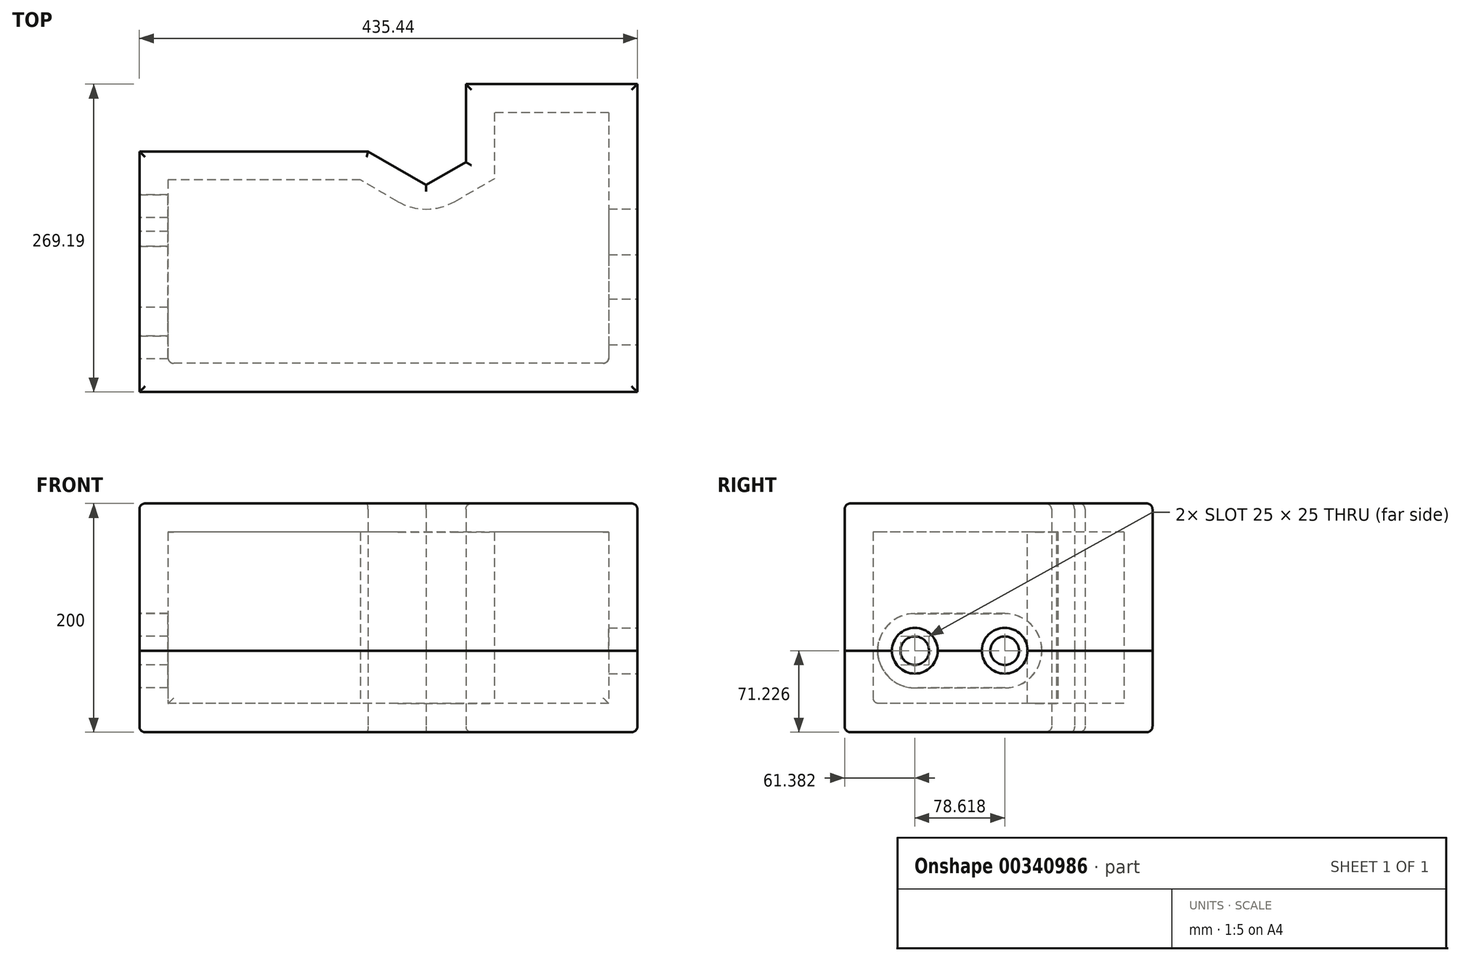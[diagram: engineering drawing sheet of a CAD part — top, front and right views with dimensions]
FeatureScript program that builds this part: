
annotation { "Feature Type Name" : "Feature", "Feature Type Description" : "" }
export const myFeature = defineFeature(function(context is Context, id is Id, definition is map)
    precondition{}
    {
        {
            var Q0;
            Q0=qCreatedBy(makeId("Top.planeOp"),FACE);
            var sketch = newSketch(context, id + "F0", { "sketchPlane" : qUnion([Q0])});
            skLineSegment(sketch, "E0.top", {"start": v(217.72, -95) * mm, "end": v(-217.72, -95) * mm});
            skLineSegment(sketch, "E0.left", {"start": v(217.72, 95) * mm, "end": v(217.72, -95) * mm});
            skLineSegment(sketch, "E0.right", {"start": v(-217.72, 95) * mm, "end": v(-217.72, -95) * mm});
            skPoint(sketch, "E0.middle", {"position": v(0, 0) * mm});
            skLineSegment(sketch, "E1", {"start": v(217.72, 174.19) * mm, "end": v(217.72, 95) * mm});
            skLineSegment(sketch, "E2", {"start": v(33.07, 86) * mm, "end": v(67.72, 106) * mm});
            skLineSegment(sketch, "E3", {"start": v(33.07, 86) * mm, "end": v(61.6, 86) * mm, "construction": true});
            skLineSegment(sketch, "E4", {"start": v(67.72, 106) * mm, "end": v(131.32, 106) * mm, "construction": true});
            skLineSegment(sketch, "E5", {"start": v(217.72, 174.19) * mm, "end": v(67.72, 174.19) * mm});
            skLineSegment(sketch, "E6", {"start": v(67.72, 174.19) * mm, "end": v(67.72, 106) * mm});
            skLineSegment(sketch, "E7", {"start": v(67.72, 106) * mm, "end": v(217.72, 106) * mm, "construction": true});
            skLineSegment(sketch, "E8", {"start": v(33.07, 86) * mm, "end": v(-17.72, 115.31) * mm});
            skLineSegment(sketch, "E9", {"start": v(33.07, 86) * mm, "end": v(7.07, 86) * mm, "construction": true});
            skLineSegment(sketch, "E10", {"start": v(-17.72, 115.31) * mm, "end": v(-217.72, 115.31) * mm});
            skLineSegment(sketch, "E11", {"start": v(-217.72, 115.31) * mm, "end": v(-217.72, 95) * mm});
            skSolve(sketch);
        }
        {
            var Q0;
            Q0=makeQuery(id+"F0.imprint","IMPRINT",FACE,{"disambiguationData":[TD([[makeQuery(id+"F0.imprint","IMPRINT",EDGE,{"derivedFrom":sQuery(id+"F0.wireOp",EDGE,"E0.top")}),-1.0]])]});
            extrude(context, id + "F1", {"entities" : qUnion([Q0]), "depth" : 200 * mm});
        }
        {
            var Q0;
            Q0=makeQuery(id+"F1.opExtrude","CAP_FACE",FACE,{"disambiguationData":[OSD([sQuery(id+"F0.wireOp",EDGE,"E0.bottom"),sQuery(id+"F0.wireOp",EDGE,"E0.top"),sQuery(id+"F0.wireOp",EDGE,"E0.left"),sQuery(id+"F0.wireOp",EDGE,"E0.right")])],"isStart":false});
            shell(context, id + "F2", {"entities" : qUnion([Q0]), "thickness" : 25 * mm});
        }
        {
            var Q0;
            Q0=makeQuery(id+"F1.opExtrude","SWEPT_FACE",FACE,{"disambiguationData":[OSD([sQuery(id+"F0.wireOp",EDGE,"E0.left")])]});
            var sketch = newSketch(context, id + "F3", { "sketchPlane" : qUnion([Q0])});
            skCircle(sketch, "E12", {"center": v(45, 71.23) * mm, "radius": 20 * mm});
            skCircle(sketch, "E13", {"center": v(-33.62, 71.23) * mm, "radius": 20 * mm});
            skLineSegment(sketch, "E14", {"start": v(-33.62, 71.23) * mm, "end": v(45, 71.23) * mm, "construction": true});
            skLineSegment(sketch, "E15", {"start": v(5.7, 71.23) * mm, "end": v(5.7, 0) * mm, "construction": true});
            skLineSegment(sketch, "E16", {"start": v(-33.62, 71.23) * mm, "end": v(-95, 71.23) * mm, "construction": true});
            skSolve(sketch);
        }
        {
            var Q0;
            Q0 = qSketchRegion(id + "F3", true);
            extrude(context, id + "F4", {"entities" : qUnion([Q0]), "operationType" : NewBodyOperationType.REMOVE, "oppositeDirection" : true, "depth" : 25 * mm});
        }
        {
            var Q0;
            Q0=makeQuery(id+"F2.opShell","OFFSET_FACE",FACE,{"disambiguationData":[OSD([sQuery(id+"F0.wireOp",EDGE,"E0.bottom"),sQuery(id+"F0.wireOp",EDGE,"E0.top"),sQuery(id+"F0.wireOp",EDGE,"E0.left"),sQuery(id+"F0.wireOp",EDGE,"E0.right")])]});
            var Q1;
            Q1=makeQuery(id+"F1.opExtrude","CAP_FACE",FACE,{"disambiguationData":[OSD([sQuery(id+"F0.wireOp",EDGE,"E0.bottom"),sQuery(id+"F0.wireOp",EDGE,"E0.top"),sQuery(id+"F0.wireOp",EDGE,"E0.left"),sQuery(id+"F0.wireOp",EDGE,"E0.right")])],"isStart":false});
            var Q2;
            Q2=makeQuery(id+"F1.opExtrude","CAP_FACE",FACE,{"disambiguationData":[OSD([sQuery(id+"F0.wireOp",EDGE,"E0.bottom"),sQuery(id+"F0.wireOp",EDGE,"E0.top"),sQuery(id+"F0.wireOp",EDGE,"E0.left"),sQuery(id+"F0.wireOp",EDGE,"E0.right")])],"isStart":true});
            fillet(context, id + "F5", {"entities" : qUnion([Q0, Q1, Q2]), "radius" : 5 * mm, "tangentPropagation" : true, "allowEdgeOverflow" : false});
        }
        {
            var Q0;
            Q0=makeQuery(id+"F1.opExtrude","SWEPT_FACE",FACE,{"disambiguationData":[OSD([sQuery(id+"F0.wireOp",EDGE,"E0.right")])]});
            var sketch = newSketch(context, id + "F6", { "sketchPlane" : qUnion([Q0])});
            skCircle(sketch, "E17", {"center": v(-45, 71.23) * mm, "radius": 12.5 * mm});
            skCircle(sketch, "E18", {"center": v(33.62, 71.23) * mm, "radius": 12.5 * mm});
            skSolve(sketch);
        }
        {
            var Q0;
            Q0 = qSketchRegion(id + "F6", true);
            extrude(context, id + "F7", {"entities" : qUnion([Q0]), "operationType" : NewBodyOperationType.REMOVE, "oppositeDirection" : true, "depth" : 25 * mm});
        }
        {
            var Q0;
            Q0=makeQuery(id+"F1.opExtrude","SWEPT_FACE",FACE,{"disambiguationData":[OSD([sQuery(id+"F0.wireOp",EDGE,"E0.top")])]});
            var sketch = newSketch(context, id + "F8", { "sketchPlane" : qUnion([Q0])});
            skPoint(sketch, "E19.middle", {"position": v(13.46, 71.23) * mm});
            skLineSegment(sketch, "E20", {"start": v(66.8, 71.23) * mm, "end": v(13.46, 71.23) * mm, "construction": true});
            skLineSegment(sketch, "E21", {"start": v(13.46, 0) * mm, "end": v(13.46, 71.23) * mm, "construction": true});
            skLineSegment(sketch, "E22.bottom", {"start": v(271.45, 71.28) * mm, "end": v(-244.53, 71.28) * mm});
            skLineSegment(sketch, "E22.top", {"start": v(271.45, 71.18) * mm, "end": v(-244.53, 71.18) * mm});
            skLineSegment(sketch, "E22.left", {"start": v(271.45, 71.28) * mm, "end": v(271.45, 71.18) * mm});
            skLineSegment(sketch, "E22.right", {"start": v(-244.53, 71.28) * mm, "end": v(-244.53, 71.18) * mm});
            skSolve(sketch);
        }
        {
            var Q0;
            Q0 = qSketchRegion(id + "F8", true);
            extrude(context, id + "F9", {"entities" : qUnion([Q0]), "operationType" : NewBodyOperationType.REMOVE, "oppositeDirection" : true, "depth" : 500 * mm});
        }
        {
            var Q0;
            Q0=makeQuery(id+"F1.opExtrude","CAP_FACE",FACE,{"disambiguationData":[OSD([sQuery(id+"F0.wireOp",EDGE,"E0.top"),sQuery(id+"F0.wireOp",EDGE,"E0.left"),sQuery(id+"F0.wireOp",EDGE,"E0.right"),sQuery(id+"F0.wireOp",EDGE,"E1"),sQuery(id+"F0.wireOp",EDGE,"E2"),sQuery(id+"F0.wireOp",EDGE,"E5"),sQuery(id+"F0.wireOp",EDGE,"E6"),sQuery(id+"F0.wireOp",EDGE,"E8"),sQuery(id+"F0.wireOp",EDGE,"E10"),sQuery(id+"F0.wireOp",EDGE,"E11")])],"isStart":false});
            var sketch = newSketch(context, id + "F10", { "sketchPlane" : qUnion([Q0])});
            skLineSegment(sketch, "E23", {"start": v(-212.72, -90) * mm, "end": v(-197.72, 95.31) * mm});
            skLineSegment(sketch, "E24", {"start": v(-197.72, 95.31) * mm, "end": v(-23.07, 95.31) * mm});
            skLineSegment(sketch, "E25", {"start": v(-23.07, 95.31) * mm, "end": v(33.07, 62.9) * mm});
            skLineSegment(sketch, "E26", {"start": v(33.07, 62.9) * mm, "end": v(87.72, 94.44) * mm});
            skLineSegment(sketch, "E27", {"start": v(87.72, 94.44) * mm, "end": v(87.72, 154.19) * mm});
            skLineSegment(sketch, "E28", {"start": v(87.72, 154.19) * mm, "end": v(197.72, 154.19) * mm});
            skLineSegment(sketch, "E29", {"start": v(197.72, 154.19) * mm, "end": v(197.72, -75) * mm});
            skLineSegment(sketch, "E30", {"start": v(197.72, -75) * mm, "end": v(-212.72, -90) * mm});
            skSolve(sketch);
        }
        {
            var Q0;
            Q0 = qSketchRegion(id + "F10", true);
            extrude(context, id + "F11", {"entities" : qUnion([Q0]), "operationType" : NewBodyOperationType.ADD, "oppositeDirection" : true, "depth" : 25 * mm});
        }
        {
            var Q0;
            {var subQ0=sQuery(id+"F0.wireOp",EDGE,"E8");var subQ1=sQuery(id+"F0.wireOp",EDGE,"E2");Q0=makeQuery(id+"F9.boolean.opBoolean","SPLIT",EDGE,{"disambiguationData":[TD([makeQuery(id+"F9.opExtrude","SWEPT_FACE",FACE,{"disambiguationData":[OSD([sQuery(id+"F8.wireOp",EDGE,"E22.top")])]})])],"derivedFrom":makeQuery(id+"F2.opShell","OFFSET_EDGE",EDGE,{"disambiguationData":[OSD([subQ1,subQ0])]})});}
            var Q1;
            {var subQ0=sQuery(id+"F0.wireOp",EDGE,"E8");var subQ1=sQuery(id+"F0.wireOp",EDGE,"E2");Q1=makeQuery(id+"F9.boolean.opBoolean","SPLIT",EDGE,{"disambiguationData":[TD([makeQuery(id+"F9.opExtrude","SWEPT_FACE",FACE,{"disambiguationData":[OSD([sQuery(id+"F8.wireOp",EDGE,"E22.bottom")])]})])],"derivedFrom":makeQuery(id+"F2.opShell","OFFSET_EDGE",EDGE,{"disambiguationData":[OSD([subQ1,subQ0])]})});}
            fillet(context, id + "F12", {"entities" : qUnion([Q0, Q1]), "radius" : 50 * mm, "tangentPropagation" : true, "allowEdgeOverflow" : false});
        }
        {
            var Q0;
            {var subQ0=sQuery(id+"F0.wireOp",EDGE,"E11");var subQ1=sQuery(id+"F0.wireOp",EDGE,"E0.right");Q0=makeQuery(id+"F9.boolean.opBoolean","SPLIT",FACE,{"disambiguationData":[TD([makeQuery(id+"F9.opExtrude","SWEPT_FACE",FACE,{"disambiguationData":[OSD([sQuery(id+"F8.wireOp",EDGE,"E22.bottom")])]})])],"derivedFrom":makeQuery(id+"F1.opExtrude","SWEPT_FACE",FACE,{"disambiguationData":[OSD([subQ1,subQ0])]})});}
            var sketch = newSketch(context, id + "F13", { "sketchPlane" : qUnion([Q0])});
            skArc(sketch, "E31", {"start": v(-45, 103.66) * mm, "mid": v(-77.43, 71.4) * mm, "end": v(-45.36, 38.8) * mm});
            skLineSegment(sketch, "E32", {"start": v(-45, 103.66) * mm, "end": v(33.62, 103.65) * mm});
            skPoint(sketch, "E32.endSnap0", {"position": v(33.62, 83.73) * mm});
            skArc(sketch, "E33", {"start": v(33.62, 38.8) * mm, "mid": v(66.05, 71.23) * mm, "end": v(33.62, 103.65) * mm});
            skLineSegment(sketch, "E34", {"start": v(-45.36, 38.8) * mm, "end": v(33.62, 38.8) * mm});
            skArc(sketch, "E35.0", {"start": v(-45, 103.76) * mm, "mid": v(-77.53, 71.4) * mm, "end": v(-45.36, 38.7) * mm});
            skLineSegment(sketch, "E35.1", {"start": v(-45, 103.76) * mm, "end": v(33.62, 103.75) * mm});
            skArc(sketch, "E35.2", {"start": v(33.62, 38.7) * mm, "mid": v(66.15, 71.23) * mm, "end": v(33.62, 103.75) * mm});
            skLineSegment(sketch, "E35.3", {"start": v(-45.36, 38.7) * mm, "end": v(33.62, 38.7) * mm});
            skSolve(sketch);
        }
        {
            var Q0;
            Q0 = qSketchRegion(id + "F13", true);
            extrude(context, id + "F14", {"entities" : qUnion([Q0]), "operationType" : NewBodyOperationType.REMOVE, "oppositeDirection" : true, "depth" : 30 * mm});
        }
        {
            var Q0;
            {var subQ0=sQuery(id+"F0.wireOp",EDGE,"E11");var subQ1=sQuery(id+"F0.wireOp",EDGE,"E0.right");Q0=makeQuery(id+"F9.boolean.opBoolean","COPY",FACE,{"disambiguationData":[TD([makeQuery(id+"F1.opExtrude","SWEPT_FACE",FACE,{"disambiguationData":[OSD([subQ1,subQ0])]}),makeQuery(id+"F2.opShell","OFFSET_FACE",FACE,{"disambiguationData":[OSD([subQ1,subQ0])]}),makeQuery(id+"F7.boolean.opBoolean","COPY",FACE,{"derivedFrom":makeQuery(id+"F7.opExtrude","SWEPT_FACE",FACE,{"disambiguationData":[OSD([sQuery(id+"F6.wireOp",EDGE,"E17")])]})}),makeQuery(id+"F7.boolean.opBoolean","COPY",FACE,{"derivedFrom":makeQuery(id+"F7.opExtrude","SWEPT_FACE",FACE,{"disambiguationData":[OSD([sQuery(id+"F6.wireOp",EDGE,"E18")])]})})])],"derivedFrom":makeQuery(id+"F9.opExtrude","SWEPT_FACE",FACE,{"disambiguationData":[OSD([sQuery(id+"F8.wireOp",EDGE,"E22.top")])]})});}
            var Q1;
            {var subQ0=sQuery(id+"F0.wireOp",EDGE,"E11");var subQ1=sQuery(id+"F0.wireOp",EDGE,"E0.right");var subQ2=makeQuery(id+"F1.opExtrude","SWEPT_FACE",FACE,{"disambiguationData":[OSD([subQ1,subQ0])]});var subQ3=makeQuery(id+"F2.opShell","OFFSET_FACE",FACE,{"disambiguationData":[OSD([subQ1,subQ0])]});var subQ4=makeQuery(id+"F7.boolean.opBoolean","COPY",FACE,{"derivedFrom":makeQuery(id+"F7.opExtrude","SWEPT_FACE",FACE,{"disambiguationData":[OSD([sQuery(id+"F6.wireOp",EDGE,"E17")])]})});var subQ5=sQuery(id+"F0.wireOp",EDGE,"E10");var subQ6=sQuery(id+"F0.wireOp",EDGE,"E2");var subQ7=sQuery(id+"F0.wireOp",EDGE,"E8");var subQ8=sQuery(id+"F0.wireOp",EDGE,"E6");var subQ9=sQuery(id+"F0.wireOp",EDGE,"E1");var subQ10=sQuery(id+"F0.wireOp",EDGE,"E0.left");var subQ11=sQuery(id+"F0.wireOp",EDGE,"E5");Q1=makeQuery(id+"F14.boolean.opBoolean","SPLIT",FACE,{"disambiguationData":[TD([subQ4])],"derivedFrom":makeQuery(id+"F9.boolean.opBoolean","COPY",FACE,{"disambiguationData":[TD([makeQuery(id+"F1.opExtrude","SWEPT_FACE",FACE,{"disambiguationData":[OSD([subQ10,subQ9])]}),subQ2,makeQuery(id+"F1.opExtrude","SWEPT_FACE",FACE,{"disambiguationData":[OSD([subQ6])]}),makeQuery(id+"F1.opExtrude","SWEPT_FACE",FACE,{"disambiguationData":[OSD([subQ11])]}),makeQuery(id+"F1.opExtrude","SWEPT_FACE",FACE,{"disambiguationData":[OSD([subQ8])]}),makeQuery(id+"F1.opExtrude","SWEPT_FACE",FACE,{"disambiguationData":[OSD([subQ7])]}),makeQuery(id+"F1.opExtrude","SWEPT_FACE",FACE,{"disambiguationData":[OSD([subQ5])]}),makeQuery(id+"F2.opShell","OFFSET_FACE",FACE,{"disambiguationData":[OSD([subQ10,subQ9])]}),subQ3,makeQuery(id+"F2.opShell","OFFSET_FACE",FACE,{"disambiguationData":[OSD([subQ6])]}),makeQuery(id+"F2.opShell","OFFSET_FACE",FACE,{"disambiguationData":[OSD([subQ11])]}),makeQuery(id+"F2.opShell","OFFSET_FACE",FACE,{"disambiguationData":[OSD([subQ8])]}),makeQuery(id+"F2.opShell","OFFSET_FACE",FACE,{"disambiguationData":[OSD([subQ7])]}),makeQuery(id+"F2.opShell","OFFSET_FACE",FACE,{"disambiguationData":[OSD([subQ5])]}),makeQuery(id+"F4.boolean.opBoolean","COPY",FACE,{"derivedFrom":makeQuery(id+"F4.opExtrude","SWEPT_FACE",FACE,{"disambiguationData":[OSD([sQuery(id+"F3.wireOp",EDGE,"E12")])]})}),subQ4])],"derivedFrom":makeQuery(id+"F9.opExtrude","SWEPT_FACE",FACE,{"disambiguationData":[OSD([sQuery(id+"F8.wireOp",EDGE,"E22.top")])]})})});}
            var Q2;
            {var subQ0=makeQuery(id+"F7.boolean.opBoolean","COPY",FACE,{"derivedFrom":makeQuery(id+"F7.opExtrude","SWEPT_FACE",FACE,{"disambiguationData":[OSD([sQuery(id+"F6.wireOp",EDGE,"E18")])]})});var subQ1=sQuery(id+"F0.wireOp",EDGE,"E0.right");var subQ2=sQuery(id+"F0.wireOp",EDGE,"E0.top");var subQ3=makeQuery(id+"F5.opFillet","BLEND_FACE",FACE,{"disambiguationData":[OSD([subQ2,subQ1]),TDD([makeQuery(id+"F2.opShell","OFFSET_EDGE",EDGE,{"disambiguationData":[OSD([subQ2,subQ1])]})])]});var subQ4=sQuery(id+"F0.wireOp",EDGE,"E11");var subQ5=makeQuery(id+"F2.opShell","OFFSET_FACE",FACE,{"disambiguationData":[OSD([subQ1,subQ4])]});var subQ6=makeQuery(id+"F1.opExtrude","SWEPT_FACE",FACE,{"disambiguationData":[OSD([subQ1,subQ4])]});var subQ7=sQuery(id+"F0.wireOp",EDGE,"E1");var subQ8=sQuery(id+"F0.wireOp",EDGE,"E0.left");Q2=makeQuery(id+"F14.boolean.opBoolean","SPLIT",FACE,{"disambiguationData":[TD([subQ0])],"derivedFrom":makeQuery(id+"F9.boolean.opBoolean","COPY",FACE,{"disambiguationData":[TD([makeQuery(id+"F1.opExtrude","SWEPT_FACE",FACE,{"disambiguationData":[OSD([subQ2])]}),makeQuery(id+"F1.opExtrude","SWEPT_FACE",FACE,{"disambiguationData":[OSD([subQ8,subQ7])]}),subQ6,makeQuery(id+"F2.opShell","OFFSET_FACE",FACE,{"disambiguationData":[OSD([subQ2])]}),makeQuery(id+"F2.opShell","OFFSET_FACE",FACE,{"disambiguationData":[OSD([subQ8,subQ7])]}),subQ5,makeQuery(id+"F4.boolean.opBoolean","COPY",FACE,{"derivedFrom":makeQuery(id+"F4.opExtrude","SWEPT_FACE",FACE,{"disambiguationData":[OSD([sQuery(id+"F3.wireOp",EDGE,"E13")])]})}),makeQuery(id+"F5.opFillet","BLEND_FACE",FACE,{"disambiguationData":[OSD([subQ2,subQ8]),TDD([makeQuery(id+"F2.opShell","OFFSET_EDGE",EDGE,{"disambiguationData":[OSD([subQ2,subQ8])]})])]}),subQ3,subQ0])],"derivedFrom":makeQuery(id+"F9.opExtrude","SWEPT_FACE",FACE,{"disambiguationData":[OSD([sQuery(id+"F8.wireOp",EDGE,"E22.top")])]})})});}
            extrude(context, id + "F15", {"entities" : qUnion([Q0, Q1, Q2]), "operationType" : NewBodyOperationType.ADD, "depth" : 0.1 * mm});
        }
    });
